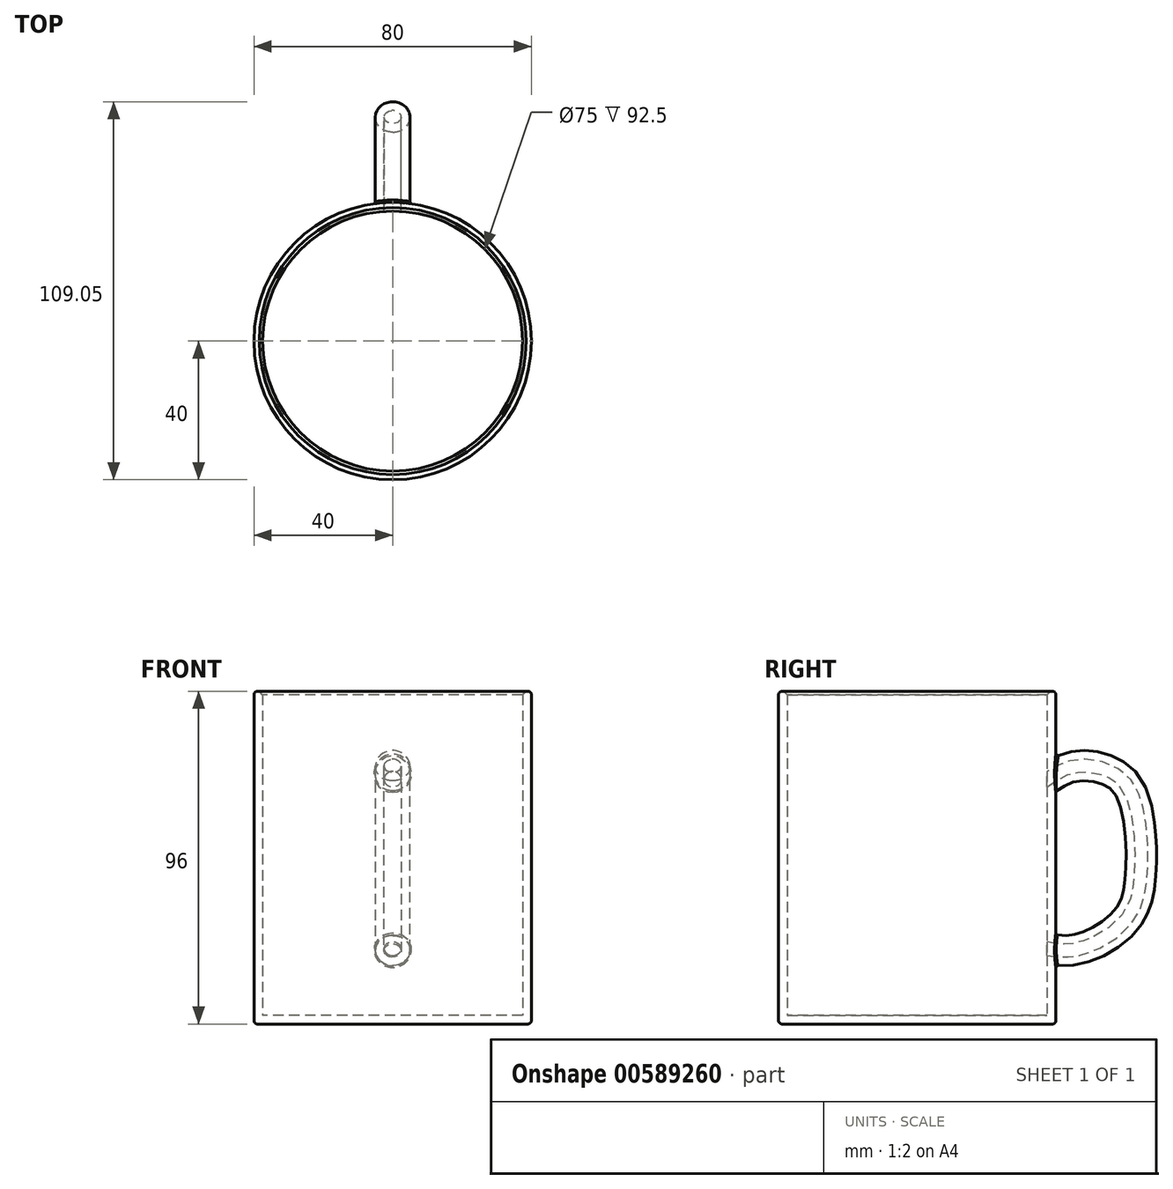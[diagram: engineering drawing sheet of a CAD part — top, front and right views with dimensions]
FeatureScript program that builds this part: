
annotation { "Feature Type Name" : "Feature", "Feature Type Description" : "" }
export const myFeature = defineFeature(function(context is Context, id is Id, definition is map)
    precondition{}
    {
        {
            var Q0;
            Q0=qCreatedBy(makeId("Top.planeOp"),FACE);
            var sketch = newSketch(context, id + "F0", { "sketchPlane" : qUnion([Q0])});
            skCircle(sketch, "E0", {"center": v(0, 0) * mm, "radius": 40 * mm});
            skSolve(sketch);
        }
        {
            var Q0;
            Q0 = qSketchRegion(id + "F0", true);
            extrude(context, id + "F1", {"entities" : qUnion([Q0]), "depth" : 96 * mm, "offsetDistance" : 25 * mm});
        }
        {
            var Q0;
            Q0=qCreatedBy(makeId("Right.planeOp"),FACE);
            var sketch = newSketch(context, id + "F2", { "sketchPlane" : qUnion([Q0])});
            skFitSpline(sketch, "E1", {"points": [v(36.75, 70.17) * mm, v(45.96, 74.24) * mm, v(57.74, 71.46) * mm, v(63.53, 60.96) * mm, v(64.39, 42.53) * mm, v(61.39, 31.82) * mm, v(53.46, 24.53) * mm, v(43.6, 21.32) * mm, v(36.1, 21.96) * mm], "startDerivative": vector(72.4, 45.6) * mm, "endDerivative": vector(-71.06, 12.72) * mm});
            skSolve(sketch);
        }
        {
            var Q0;
            Q0=qCreatedBy(makeId("Front.planeOp"),FACE);
            cPlane(context, id + "F3", {"entities" : qUnion([Q0]), "cplaneType" : CPlaneType.OFFSET, "offset" : 40 * mm, "oppositeDirection" : true, "width" : 150 * mm, "height" : 150 * mm});
        }
        {
            var Q0;
            Q0=qCreatedBy(id+"F3.planeOp",FACE);
            var sketch = newSketch(context, id + "F4", { "sketchPlane" : qUnion([Q0])});
            skCircle(sketch, "E2", {"center": v(0, 72.1) * mm, "radius": 5 * mm});
            skSolve(sketch);
        }
        {
            var Q0;
            Q0=makeQuery(id+"F4.imprint","IMPRINT",FACE,{"disambiguationData":[TD([[makeQuery(id+"F4.imprint","IMPRINT",EDGE,{"derivedFrom":sQuery(id+"F4.wireOp",EDGE,"E2")}),1.0]])]});
            var Q1;
            Q1=sQuery(id+"F2.wireOp",EDGE,"E1");
            sweep(context, id + "F5", {"operationType" : NewBodyOperationType.ADD, "profiles" : qUnion([Q0]), "path" : qUnion([Q1])});
        }
        {
            var Q0;
            Q0=makeQuery(id+"F1.opExtrude","CAP_FACE",FACE,{"disambiguationData":[OSD([sQuery(id+"F0.wireOp",EDGE,"E0")])],"isStart":false});
            shell(context, id + "F6", {"entities" : qUnion([Q0]), "thickness" : 2.5 * mm});
        }
        {
            var Q0;
            Q0=makeQuery(id+"F1.opExtrude","CAP_EDGE",EDGE,{"disambiguationData":[OSD([sQuery(id+"F0.wireOp",EDGE,"E0")])],"isStart":false});
            fillet(context, id + "F7", {"entities" : qUnion([Q0]), "radius" : 1 * mm, "tangentPropagation" : true, "allowEdgeOverflow" : false});
        }
        {
            var Q0;
            {var subQ0=sQuery(id+"F0.wireOp",EDGE,"E0");Q0=makeQuery(id+"F6.opShell","OFFSET_EDGE",EDGE,{"disambiguationData":[OSD([subQ0]),TDD([makeQuery(id+"F1.opExtrude","CAP_EDGE",EDGE,{"disambiguationData":[OSD([subQ0])],"isStart":false})])]});}
            chamfer(context, id + "F8", {"entities" : qUnion([Q0]), "width" : 1 * mm, "tangentPropagation" : true});
        }
        {
            var Q0;
            Q0=makeQuery(id+"F5.opSweep","SWEPT_FACE",FACE,{"disambiguationData":[OSD([sQuery(id+"F2.wireOp",EDGE,"E1"),sQuery(id+"F4.wireOp",EDGE,"E2")])]});
            chamfer(context, id + "F9", {"entities" : qUnion([Q0]), "width" : .5 * mm, "tangentPropagation" : true});
        }
        {
            var Q0;
            Q0=makeQuery(id+"F1.opExtrude","CAP_EDGE",EDGE,{"disambiguationData":[OSD([sQuery(id+"F0.wireOp",EDGE,"E0")])],"isStart":true});
            fillet(context, id + "F10", {"entities" : qUnion([Q0]), "radius" : 1 * mm, "tangentPropagation" : true, "allowEdgeOverflow" : false});
        }
    });
